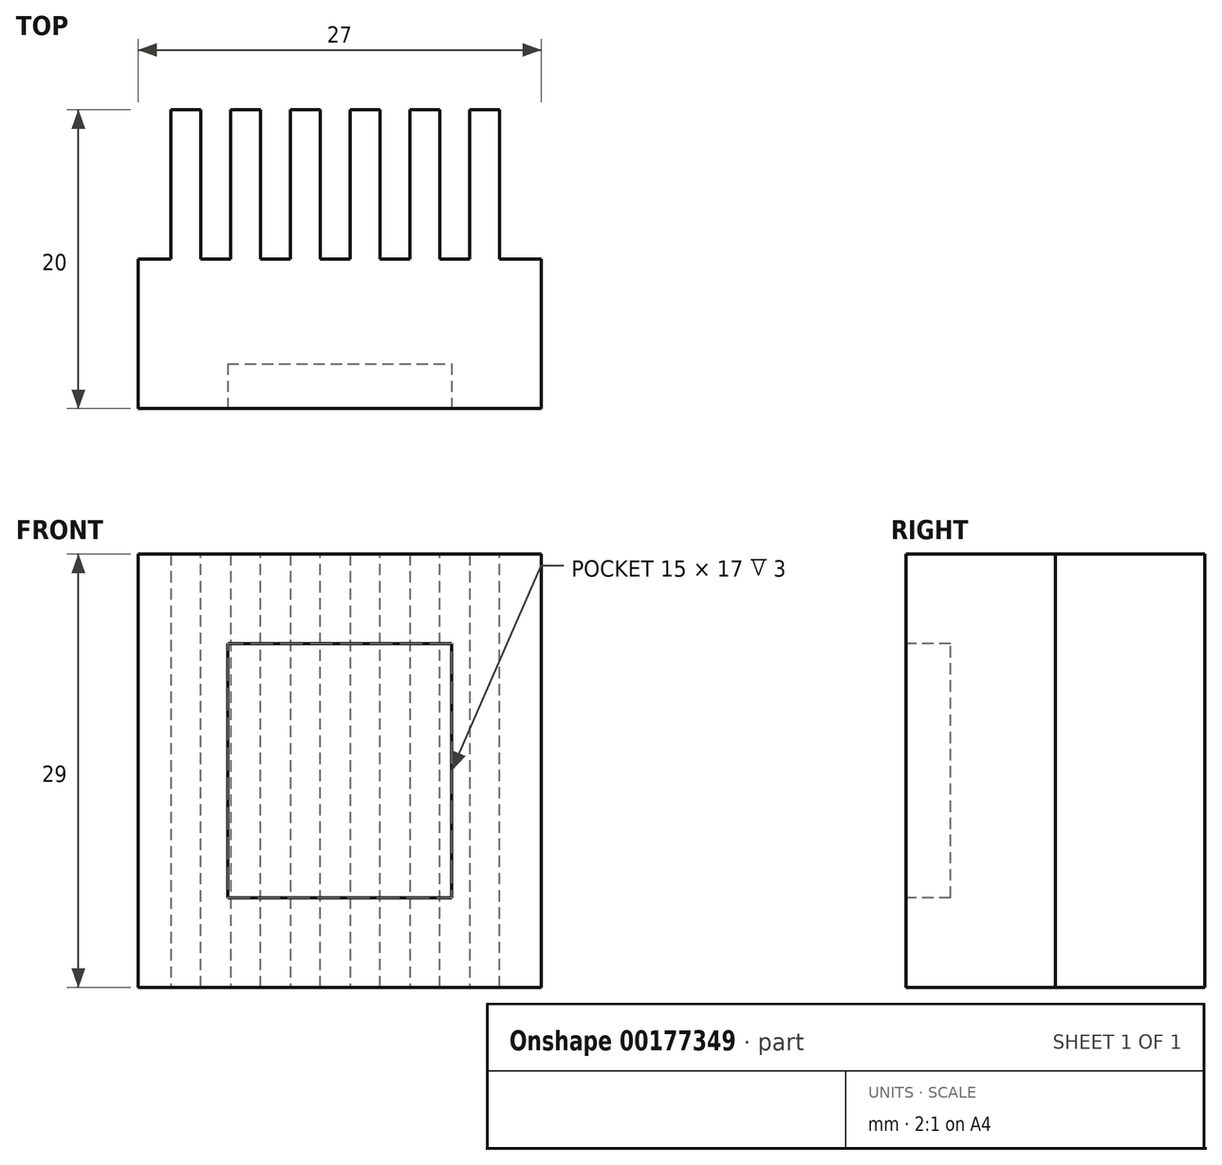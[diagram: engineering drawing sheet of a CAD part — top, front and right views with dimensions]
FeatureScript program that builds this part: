
annotation { "Feature Type Name" : "Feature", "Feature Type Description" : "" }
export const myFeature = defineFeature(function(context is Context, id is Id, definition is map)
    precondition{}
    {
        {
            var Q0;
            Q0=qCreatedBy(makeId("Top.planeOp"),FACE);
            var sketch = newSketch(context, id + "F0", { "sketchPlane" : qUnion([Q0])});
            skLineSegment(sketch, "E0.bottom", {"start": v(0, 0) * mm, "end": v(27, 0) * mm});
            skLineSegment(sketch, "E0.top", {"start": v(0, 20) * mm, "end": v(27, 20) * mm});
            skLineSegment(sketch, "E0.left", {"start": v(0, 0) * mm, "end": v(0, 20) * mm});
            skLineSegment(sketch, "E0.right", {"start": v(27, 0) * mm, "end": v(27, 20) * mm});
            skSolve(sketch);
        }
        {
            var Q0;
            Q0 = qSketchRegion(id + "F0", true);
            extrude(context, id + "F1", {"entities" : qUnion([Q0]), "depth" : 29 * mm, "offsetDistance" : 25 * mm});
        }
        {
            var Q0;
            Q0=makeQuery(id+"F1.opExtrude","CAP_FACE",FACE,{"disambiguationData":[OSD([sQuery(id+"F0.wireOp",EDGE,"E0.bottom"),sQuery(id+"F0.wireOp",EDGE,"E0.top"),sQuery(id+"F0.wireOp",EDGE,"E0.left"),sQuery(id+"F0.wireOp",EDGE,"E0.right")])],"isStart":false});
            var sketch = newSketch(context, id + "F2", { "sketchPlane" : qUnion([Q0])});
            skLineSegment(sketch, "E1", {"start": v(-5.66, 10) * mm, "end": v(2.2, 10) * mm});
            skLineSegment(sketch, "E2", {"start": v(2.2, 10) * mm, "end": v(2.2, 21) * mm});
            skLineSegment(sketch, "E3", {"start": v(2.2, 21) * mm, "end": v(4.2, 21) * mm});
            skLineSegment(sketch, "E4", {"start": v(4.2, 21) * mm, "end": v(4.2, 10) * mm});
            skLineSegment(sketch, "E5", {"start": v(4.2, 10) * mm, "end": v(6.2, 10) * mm});
            skLineSegment(sketch, "E6.1.0.0", {"start": v(6.2, 21) * mm, "end": v(8.2, 21) * mm});
            skLineSegment(sketch, "E6.1.0.1", {"start": v(8.2, 21) * mm, "end": v(8.2, 10) * mm});
            skLineSegment(sketch, "E6.1.0.2", {"start": v(6.2, 10) * mm, "end": v(6.2, 21) * mm});
            skLineSegment(sketch, "E6.1.0.3", {"start": v(8.2, 10) * mm, "end": v(10.2, 10) * mm});
            skLineSegment(sketch, "E6.2.0.0", {"start": v(10.2, 21) * mm, "end": v(12.2, 21) * mm});
            skLineSegment(sketch, "E6.2.0.1", {"start": v(12.2, 21) * mm, "end": v(12.2, 10) * mm});
            skLineSegment(sketch, "E6.2.0.2", {"start": v(10.2, 10) * mm, "end": v(10.2, 21) * mm});
            skLineSegment(sketch, "E6.2.0.3", {"start": v(12.2, 10) * mm, "end": v(14.2, 10) * mm});
            skLineSegment(sketch, "E6.3.0.0", {"start": v(14.2, 21) * mm, "end": v(16.2, 21) * mm});
            skLineSegment(sketch, "E6.3.0.1", {"start": v(16.2, 21) * mm, "end": v(16.2, 10) * mm});
            skLineSegment(sketch, "E6.3.0.2", {"start": v(14.2, 10) * mm, "end": v(14.2, 21) * mm});
            skLineSegment(sketch, "E6.3.0.3", {"start": v(16.2, 10) * mm, "end": v(18.2, 10) * mm});
            skLineSegment(sketch, "E6.4.0.0", {"start": v(18.2, 21) * mm, "end": v(20.2, 21) * mm});
            skLineSegment(sketch, "E6.4.0.1", {"start": v(20.2, 21) * mm, "end": v(20.2, 10) * mm});
            skLineSegment(sketch, "E6.4.0.2", {"start": v(18.2, 10) * mm, "end": v(18.2, 21) * mm});
            skLineSegment(sketch, "E6.4.0.3", {"start": v(20.2, 10) * mm, "end": v(22.2, 10) * mm});
            skLineSegment(sketch, "E6.direction1", {"start": v(1.5, 21) * mm, "end": v(5.5, 21) * mm, "construction": true});
            skLineSegment(sketch, "E7.0.5.0", {"start": v(22.2, 21) * mm, "end": v(24.2, 21) * mm});
            skLineSegment(sketch, "E7.3.5.0", {"start": v(24.2, 21) * mm, "end": v(24.2, 10) * mm});
            skLineSegment(sketch, "E7.6.5.0", {"start": v(22.2, 10) * mm, "end": v(22.2, 21) * mm});
            skLineSegment(sketch, "E7.9.5.0", {"start": v(24.2, 10) * mm, "end": v(26.2, 10) * mm});
            skLineSegment(sketch, "E8", {"start": v(26.2, 10) * mm, "end": v(30.42, 10) * mm});
            skLineSegment(sketch, "E9", {"start": v(30.42, 10) * mm, "end": v(30.42, 25.21) * mm});
            skLineSegment(sketch, "E10", {"start": v(30.42, 25.21) * mm, "end": v(-5.88, 25.21) * mm});
            skLineSegment(sketch, "E11", {"start": v(-5.88, 25.21) * mm, "end": v(-5.66, 10) * mm});
            skSolve(sketch);
        }
        {
            var Q0;
            Q0 = qSketchRegion(id + "F2", true);
            extrude(context, id + "F3", {"entities" : qUnion([Q0]), "operationType" : NewBodyOperationType.REMOVE, "endBound" : BoundingType.THROUGH_ALL, "oppositeDirection" : true, "depth" : 25 * mm, "offsetDistance" : 25 * mm});
        }
        {
            var Q0;
            Q0=makeQuery(id+"F1.opExtrude","SWEPT_FACE",FACE,{"disambiguationData":[OSD([sQuery(id+"F0.wireOp",EDGE,"E0.bottom")])]});
            var sketch = newSketch(context, id + "F4", { "sketchPlane" : qUnion([Q0])});
            skLineSegment(sketch, "E12.bottom", {"start": v(6, 6) * mm, "end": v(21, 6) * mm});
            skLineSegment(sketch, "E12.top", {"start": v(6, 23) * mm, "end": v(21, 23) * mm});
            skLineSegment(sketch, "E12.left", {"start": v(6, 6) * mm, "end": v(6, 23) * mm});
            skLineSegment(sketch, "E12.right", {"start": v(21, 6) * mm, "end": v(21, 23) * mm});
            skSolve(sketch);
        }
        {
            var Q0;
            Q0 = qSketchRegion(id + "F4", true);
            extrude(context, id + "F5", {"entities" : qUnion([Q0]), "operationType" : NewBodyOperationType.REMOVE, "oppositeDirection" : true, "depth" : 3 * mm, "offsetDistance" : 25 * mm});
        }
    });
